# Revit family: Faucet_Vessel-Lavatory-DXV-Randall-D351021XX_Series
name_source: partatom
category: Plumbing Fixtures
revit_build: Autodesk Revit 2014 (Build: 20130308_1515(x64)
units: mm (PartAtom-declared; Revit-internal decimal feet)

## types (12) — shared parameters
ADA Compliant = Yes
Assembly Code = D2020300
CW Connection = Yes
CWFU = 1.5
Cold Water Connection Diameter = 3/8"
Default Elevation = 0"
HW Connection = Yes
HWFU = 1.5
Height = 12 5/16"
Hot Water Connection Diameter = 0"
Installation Type = Deck Mounted
Length = 6"
Manufacturer = DXV
Price = Prices may vary. Please consult Manufacturer Representative for most up-to-date price list.
Product Documentation Link = https://dxv01.blob.core.windows.net
Product Page URL = https://www.dxv.com
Revised Date = 28/09/2017
URL = http://www.dxv.com
Vent Connection = No
WFU = 2
Warranty Documentation Link = https://www.dxv.com
Width = 3 1/16"

## per-type parameters (varying)
| type | Description | Finish | Flow Rate | Material | Model | Pop-up drain handle | Waste Connection |
| D35102150.150 | Randall Vessel Faucets Without Drain | Metal-DXV-150-Platinum Nickel | 1.5 GPM (5.7 L/min.) | Metal-DXV-150-Platinum Nickel | D35102150.150 | No | Yes |
| D35102150.100 | Randall Vessel Faucets,Without Drain | Metal-DXV-100-Polished Chrome | 1.5 GPM (5.7 L/min.) | Metal-DXV-100-Polished Chrome | D35102150.100 | No | Yes |
| D35102150.144 | Randall Vessel Faucets Without Drain | Metal-DXV-144-Brushed Nickel | 1.5 GPM (5.7 L/min.) | Metal-DXV-144-Brushed Nickel | D35102150.144 | No | Yes |
| D3510215C.100 | Randall Vessel Faucets Without Drain | Metal-DXV-100-Polished Chrome | 1.2 GPM (4.5 L/min.) | Metal-DXV-100-Polished Chrome | D3510215C.100 | No | No |
| D3510215C.144 | Randall Vessel Faucets Without Drain | Metal-DXV-144-Brushed Nickel | 1.2 GPM (4.5 L/min.) | Metal-DXV-144-Brushed Nickel | D3510215C.144 | No | No |
| D3510215C.150 | Randall Vessel Faucets Without Drain | Metal-DXV-150-Platinum Nickel | 1.2 GPM (4.5 L/min.) | Metal-DXV-150-Platinum Nickel | D3510216C.150 | No | No |
| D35102151.100 | Randall Vessel Faucets With Drain | Metal-DXV-100-Polished Chrome | 1.5 GPM (5.7 L/min.) | Metal-DXV-100-Polished Chrome | D35102151.100 | Yes | No |
| D35102151.144 | Randall Vessel Faucets With Drain | Metal-DXV-144-Brushed Nickel | 1.5 GPM (5.7 L/min.) | Metal-DXV-144-Brushed Nickel | D35102151.144 | Yes | No |
| D35102151.150 | Randall Vessel Faucets With Drain | Metal-DXV-150-Platinum Nickel | 1.5 GPM (5.7 L/min.) | Metal-DXV-150-Platinum Nickel | D35102151.150 | Yes | No |
| D3510216C.100 | Randall Vessel Faucets With Drain | Metal-DXV-100-Polished Chrome | 1.2 GPM (4.5 L/min.) | Metal-DXV-100-Polished Chrome | D3510216C.100 | Yes | No |
| D3510216C.144 | Randall Vessel Faucets With Drain | Metal-DXV-144-Brushed Nickel | 1.2 GPM (4.5 L/min.) | Metal-DXV-144-Brushed Nickel | D3510216C.144 | Yes | No |
| D3510216C.150 | Randall Vessel Faucets With Drain | Metal-DXV-150-Platinum Nickel | 1.2 GPM (4.5 L/min.) | Metal-DXV-150-Platinum Nickel | D3510216C.150 | Yes | No |

## geometry (parser evidence)
native form markers: Sweep x1
no freeform markers — native parametric forms only
